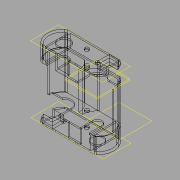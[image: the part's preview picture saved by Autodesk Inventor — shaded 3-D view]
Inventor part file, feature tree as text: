
AUTODESK INVENTOR PART (.ipt)
format: ipt  version: 2015 (Build 190159000, 159)  size: 471,040 bytes
history: native  units: mm
features: sketch x15, extrude x15, plane x8, reference x2
ambient origin geometry x8: Origin, YZ Plane, XZ Plane, XY Plane, X Axis, Y Axis, Z Axis, Center Point
bodies: Body1 (feature_tree), Body2 (feature_tree)
feature tree (40):
  sketch  "Sketch2"  dims[d13=1.0mm d14=0.0mm d15=2.0mm d16=0.0mm]
  plane  "Work Plane5"
  sketch  "Sketch5"  dims[d25=1.0mm d26=0.0mm d30=1.0mm d31=0.0mm]
  plane  "Work Plane1"
  extrude  "Extrusion3"  Depth=2.0mm TaperAngle=0.0deg
  plane  "Work Plane4"
  extrude  "Extrusion4"  Depth=1.0mm TaperAngle=0.0deg
  plane  "Work Plane6"
  sketch  "Sketch7"  dims[d47=4.0mm d48=1.0mm d49=0.0mm]
  plane  "Work Plane2"
  extrude  "Extrusion8"  Depth=8.75mm
  extrude  "Extrusion10"  Depth=1.0mm TaperAngle=0.0deg
  plane  "Work Plane12"
  plane  "Work Plane13"
  extrude  "Extrusion12"  Depth=1.0mm TaperAngle=0.0deg
  plane  "Work Plane14"
  extrude  "Extrusion13"  Depth=1.0mm TaperAngle=0.0deg
  extrude  "Extrusion14"  Depth=1.0mm TaperAngle=0.0deg
  extrude  "Extrusion15"  Depth=3.25mm TaperAngle=0.0deg
  extrude  "Extrusion16"  Depth=3.25mm TaperAngle=0.0deg
  extrude  "Extrusion17"  Depth=1.0mm
  extrude  "Extrusion18"  Depth=1.0mm
  extrude  "Extrusion19"  Depth=1.0mm TaperAngle=0.0deg
  extrude  "Extrusion20"  [1 undecoded]
  extrude  "Extrusion21"  [1 undecoded]
  extrude  "Extrusion22"  [1 undecoded]
  reference  "Reference72"
  sketch  "Sketch6"  dims[d40=8.75mm d45=8.75mm]
  sketch  "Sketch18"  dims[d50=8.75mm d52=1.0mm d53=0.0mm]
  reference  "Reference151"
  sketch  "Sketch19"  dims[d55=1.0mm d56=1.0mm d57=0.0mm]
  sketch  "Sketch21"  dims[d59=1.0mm d60=1.0mm d61=0.0mm]
  sketch  "Sketch23"  dims[d62=1.0mm d63=0.0mm d65=3.25mm d66=0.0mm]
  sketch  "Sketch24"  dims[d67=1.0mm d68=0.0mm d70=3.25mm d71=0.0mm]
  sketch  "Sketch25"  dims[d72=1.0mm d73=0.0mm d76=1.0mm]
  sketch  "Sketch26"  dims[d77=1.0mm d78=0.0mm d79=1.0mm]
  sketch  "Sketch27"  dims[d80=1.0mm d81=1.0mm d82=0.0mm]
  sketch  "Sketch28"
  sketch  "Sketch29"
  sketch  "Sketch30"
note: 3 required parameter values undecoded (feature->parameter linkage not recoverable at this tier; creation-order binding heuristic only, values carry confidence <= 0.55)
